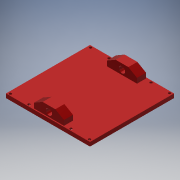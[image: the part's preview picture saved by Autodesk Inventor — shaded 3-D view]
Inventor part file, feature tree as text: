
AUTODESK INVENTOR PART (.ipt)
format: ipt  version: 2018 (Build 220112000, 112)  size: 192,512 bytes
history: native  units: in
note: dims shown in document units (in); Inventor stores cm internally (conversion verified against a paired STEP export)
features: sketch x6, extrude x5, hole x1, projected_geometry x1
ambient origin geometry x8: Origin, YZ Plane, XZ Plane, XY Plane, X Axis, Y Axis, Z Axis, Center Point
bodies: Solid1 (feature_tree)
feature tree (13):
  extrude  "Extrusion1"  Depth=4.0in
  extrude  "Extrusion2"  Depth=3.0in
  extrude  "Extrusion3"  Depth=3.0in
  extrude  "Extrusion4"  Depth=3.0in TaperAngle=0.0deg
  extrude  "Extrusion5"  Depth=2.5in
  hole  "Hole1"  [1 undecoded]
  sketch  "Sketch1"  dims[d0=84.0in d1=4.0in]
  sketch  "Sketch2"  dims[d2=84.0in d3=0.0in d4=3.0in]
  projected_geometry  "Projected Loop1"
  sketch  "Sketch3"  dims[d5=3.0in d6=3.0in]
  sketch  "Sketch4"  dims[d7=3.0in d8=3.0in d9=0.0in]
  sketch  "Sketch5"  dims[d17=2.5in d18=2.5in]
  sketch  "Sketch6"  dims[d19=2.0in d20=0.7874in d22=80.0in d23=0.7874in d25=79.0in d28=2.5in d29=21.0in d30=2.0in d31=0.7874in d33=80.0in d34=0.7874in d36=42.0in d39=3.0in d40=0.0in d42=5.0in d43=10.0in d45=82.0in d46=0.0in d47=64.0in d48=82.0in d49=0.0in d50=30.0in d51=8.0in d52=8.5in d53=6.288in d54=0.75in d55=0.375in d56=0.25in d57=0.5635in d58=1.0in d59=0.8108in d60=150.0deg]
note: 1 required parameter value undecoded (feature->parameter linkage not recoverable at this tier; creation-order binding heuristic only, values carry confidence <= 0.55)
